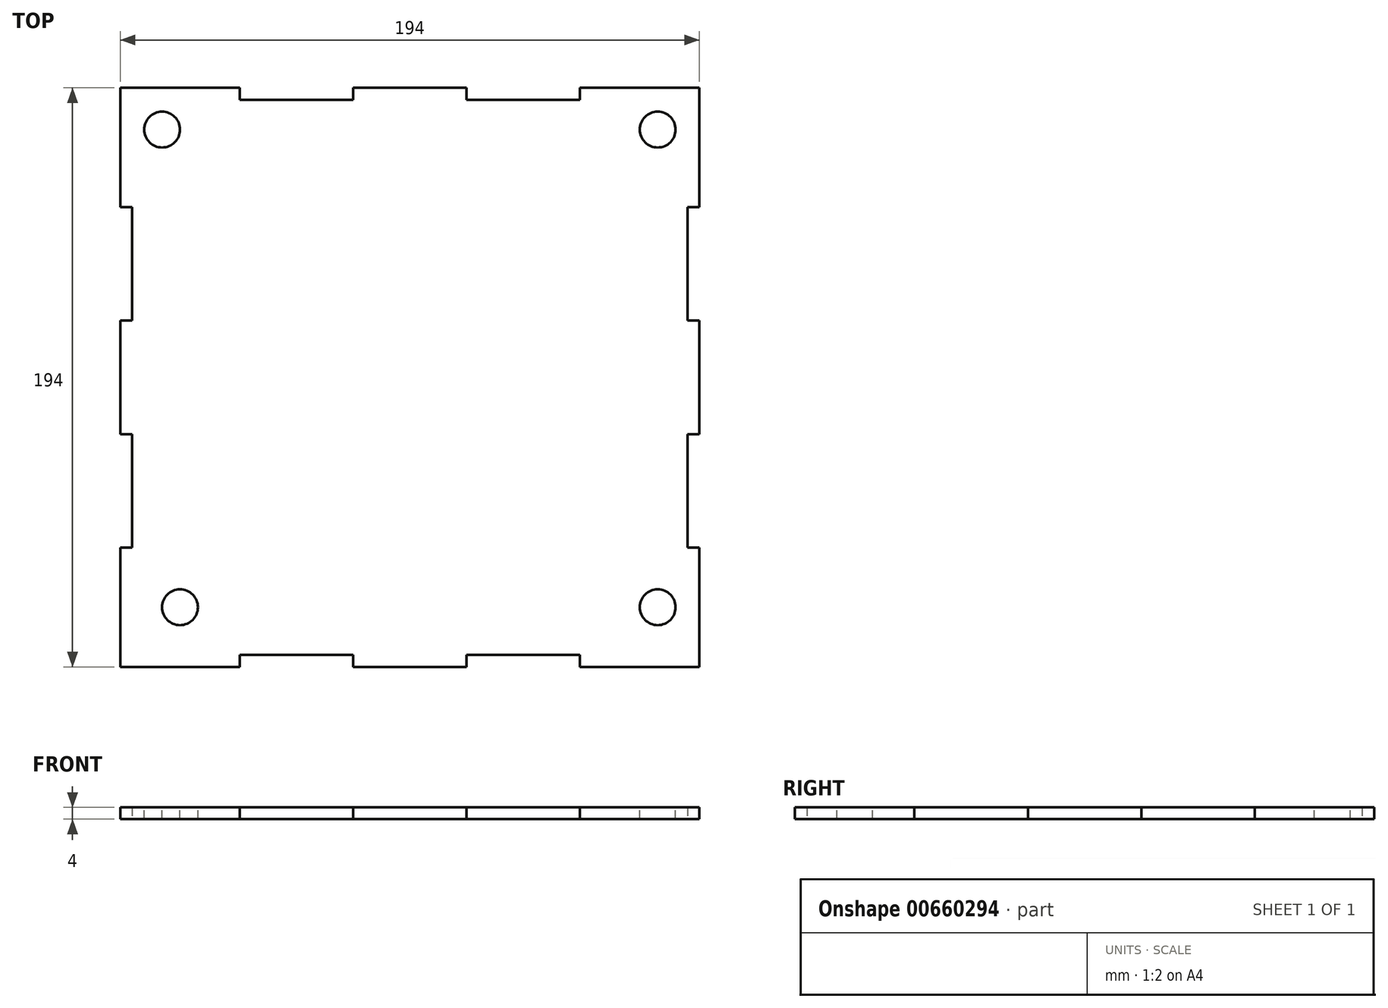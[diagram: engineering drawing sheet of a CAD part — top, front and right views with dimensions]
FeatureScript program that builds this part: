
annotation { "Feature Type Name" : "Feature", "Feature Type Description" : "" }
export const myFeature = defineFeature(function(context is Context, id is Id, definition is map)
    precondition{}
    {
        {
            var Q0;
            Q0=qCreatedBy(makeId("Top.planeOp"),FACE);
            var sketch = newSketch(context, id + "F0", { "sketchPlane" : qUnion([Q0])});
            skLineSegment(sketch, "E0.bottom", {"start": v(0, 0) * mm, "end": v(194, 0) * mm});
            skLineSegment(sketch, "E0.top", {"start": v(0, 194) * mm, "end": v(194, 194) * mm});
            skLineSegment(sketch, "E0.left", {"start": v(0, 0) * mm, "end": v(0, 194) * mm});
            skLineSegment(sketch, "E0.right", {"start": v(194, 0) * mm, "end": v(194, 194) * mm});
            skLineSegment(sketch, "E1.bottom", {"start": v(40, 0) * mm, "end": v(78, 0) * mm});
            skLineSegment(sketch, "E1.top", {"start": v(40, 4) * mm, "end": v(78, 4) * mm});
            skLineSegment(sketch, "E1.left", {"start": v(40, 0) * mm, "end": v(40, 4) * mm});
            skLineSegment(sketch, "E1.right", {"start": v(78, 0) * mm, "end": v(78, 4) * mm});
            skLineSegment(sketch, "E2.bottom", {"start": v(116, 0) * mm, "end": v(154, 0) * mm});
            skLineSegment(sketch, "E2.top", {"start": v(116, 4) * mm, "end": v(154, 4) * mm});
            skLineSegment(sketch, "E2.left", {"start": v(116, 0) * mm, "end": v(116, 4) * mm});
            skLineSegment(sketch, "E2.right", {"start": v(154, 0) * mm, "end": v(154, 4) * mm});
            skLineSegment(sketch, "E3.bottom", {"start": v(40, 194) * mm, "end": v(78, 194) * mm});
            skLineSegment(sketch, "E3.top", {"start": v(40, 190) * mm, "end": v(78, 190) * mm});
            skLineSegment(sketch, "E3.left", {"start": v(40, 194) * mm, "end": v(40, 190) * mm});
            skLineSegment(sketch, "E3.right", {"start": v(78, 194) * mm, "end": v(78, 190) * mm});
            skLineSegment(sketch, "E4.bottom", {"start": v(116, 194) * mm, "end": v(154, 194) * mm});
            skLineSegment(sketch, "E4.top", {"start": v(116, 190) * mm, "end": v(154, 190) * mm});
            skLineSegment(sketch, "E4.left", {"start": v(116, 194) * mm, "end": v(116, 190) * mm});
            skLineSegment(sketch, "E4.right", {"start": v(154, 194) * mm, "end": v(154, 190) * mm});
            skLineSegment(sketch, "E5.bottom", {"start": v(0, 154) * mm, "end": v(4, 154) * mm});
            skLineSegment(sketch, "E5.top", {"start": v(0, 116) * mm, "end": v(4, 116) * mm});
            skLineSegment(sketch, "E5.left", {"start": v(0, 154) * mm, "end": v(0, 116) * mm});
            skLineSegment(sketch, "E5.right", {"start": v(4, 154) * mm, "end": v(4, 116) * mm});
            skLineSegment(sketch, "E6.bottom", {"start": v(0, 78) * mm, "end": v(4, 78) * mm});
            skLineSegment(sketch, "E6.top", {"start": v(0, 40) * mm, "end": v(4, 40) * mm});
            skLineSegment(sketch, "E6.left", {"start": v(0, 78) * mm, "end": v(0, 40) * mm});
            skLineSegment(sketch, "E6.right", {"start": v(4, 78) * mm, "end": v(4, 40) * mm});
            skLineSegment(sketch, "E7.bottom", {"start": v(194, 154) * mm, "end": v(190, 154) * mm});
            skLineSegment(sketch, "E7.top", {"start": v(194, 116) * mm, "end": v(190, 116) * mm});
            skLineSegment(sketch, "E7.left", {"start": v(194, 154) * mm, "end": v(194, 116) * mm});
            skLineSegment(sketch, "E7.right", {"start": v(190, 154) * mm, "end": v(190, 116) * mm});
            skLineSegment(sketch, "E8.bottom", {"start": v(194, 78) * mm, "end": v(190, 78) * mm});
            skLineSegment(sketch, "E8.top", {"start": v(194, 40) * mm, "end": v(190, 40) * mm});
            skLineSegment(sketch, "E8.left", {"start": v(194, 78) * mm, "end": v(194, 40) * mm});
            skLineSegment(sketch, "E8.right", {"start": v(190, 78) * mm, "end": v(190, 40) * mm});
            skSolve(sketch);
        }
        {
            var Q0;
            Q0=makeQuery(id+"F0.imprint","IMPRINT",FACE,{"disambiguationData":[TD([[makeQuery(id+"F0.imprint","IMPRINT",EDGE,{"derivedFrom":sQuery(id+"F0.wireOp",EDGE,"E1.top")}),1.0]])]});
            extrude(context, id + "F1", {"entities" : qUnion([Q0]), "depth" : 4 * mm, "offsetDistance" : 25 * mm});
        }
        {
            var Q0;
            Q0=makeQuery(id+"F1.opExtrude","CAP_FACE",FACE,{"disambiguationData":[OSD([sQuery(id+"F0.wireOp",EDGE,"E0.bottom"),sQuery(id+"F0.wireOp",EDGE,"E0.top"),sQuery(id+"F0.wireOp",EDGE,"E0.left"),sQuery(id+"F0.wireOp",EDGE,"E0.right"),sQuery(id+"F0.wireOp",EDGE,"E1.top"),sQuery(id+"F0.wireOp",EDGE,"E1.left"),sQuery(id+"F0.wireOp",EDGE,"E1.right"),sQuery(id+"F0.wireOp",EDGE,"E2.top"),sQuery(id+"F0.wireOp",EDGE,"E2.left"),sQuery(id+"F0.wireOp",EDGE,"E2.right"),sQuery(id+"F0.wireOp",EDGE,"E3.top"),sQuery(id+"F0.wireOp",EDGE,"E3.left"),sQuery(id+"F0.wireOp",EDGE,"E3.right"),sQuery(id+"F0.wireOp",EDGE,"E4.top"),sQuery(id+"F0.wireOp",EDGE,"E4.left"),sQuery(id+"F0.wireOp",EDGE,"E4.right"),sQuery(id+"F0.wireOp",EDGE,"E5.bottom"),sQuery(id+"F0.wireOp",EDGE,"E5.top"),sQuery(id+"F0.wireOp",EDGE,"E5.right"),sQuery(id+"F0.wireOp",EDGE,"E6.bottom"),sQuery(id+"F0.wireOp",EDGE,"E6.top"),sQuery(id+"F0.wireOp",EDGE,"E6.right"),sQuery(id+"F0.wireOp",EDGE,"E7.bottom"),sQuery(id+"F0.wireOp",EDGE,"E7.top"),sQuery(id+"F0.wireOp",EDGE,"E7.right"),sQuery(id+"F0.wireOp",EDGE,"E8.bottom"),sQuery(id+"F0.wireOp",EDGE,"E8.top"),sQuery(id+"F0.wireOp",EDGE,"E8.right")])],"isStart":false});
            var sketch = newSketch(context, id + "F2", { "sketchPlane" : qUnion([Q0])});
            skCircle(sketch, "E9", {"center": v(14, 180) * mm, "radius": 6 * mm});
            skCircle(sketch, "E10", {"center": v(180, 180) * mm, "radius": 6 * mm});
            skCircle(sketch, "E11", {"center": v(20, 20) * mm, "radius": 6 * mm});
            skCircle(sketch, "E12", {"center": v(180, 20) * mm, "radius": 6 * mm});
            skSolve(sketch);
        }
        {
            var Q0;
            Q0=makeQuery(id+"F2.imprint","IMPRINT",FACE,{"disambiguationData":[TD([[makeQuery(id+"F2.imprint","IMPRINT",EDGE,{"derivedFrom":sQuery(id+"F2.wireOp",EDGE,"E9")}),1.0]])]});
            var Q1;
            Q1=makeQuery(id+"F2.imprint","IMPRINT",FACE,{"disambiguationData":[TD([[makeQuery(id+"F2.imprint","IMPRINT",EDGE,{"derivedFrom":sQuery(id+"F2.wireOp",EDGE,"E10")}),1.0]])]});
            var Q2;
            Q2=makeQuery(id+"F2.imprint","IMPRINT",FACE,{"disambiguationData":[TD([[makeQuery(id+"F2.imprint","IMPRINT",EDGE,{"derivedFrom":sQuery(id+"F2.wireOp",EDGE,"E12")}),1.0]])]});
            var Q3;
            Q3=makeQuery(id+"F2.imprint","IMPRINT",FACE,{"disambiguationData":[TD([[makeQuery(id+"F2.imprint","IMPRINT",EDGE,{"derivedFrom":sQuery(id+"F2.wireOp",EDGE,"E11")}),1.0]])]});
            extrude(context, id + "F3", {"entities" : qUnion([Q0, Q1, Q2, Q3]), "operationType" : NewBodyOperationType.REMOVE, "oppositeDirection" : true, "depth" : 4 * mm, "offsetDistance" : 25 * mm});
        }
    });
